# Revit family: PRD_FrankeWS_TltRllHldrs_Heavy-DutyToiletRollHolder_HDTX0001
name_source: partatom
category: Specialty Equipment
revit_build: Autodesk Revit 2018 (Build: 20190510_1515(x64)
units: mm (PartAtom-declared; Revit-internal decimal feet)

## family parameters
Cut with Voids When Loaded = No
Host = Face
OmniClass Number = 23.40.20.21.21
OmniClass Title = Toilet Paper Dispensers
Part Type = Normal
Room Calculation Point = No
Round Connector Dimension = Use Diameter
Shared = No

## types (1)
- HDTX0001
    AssetType = Fixed
    BIMObjectName = PRD_AR_ToiletRollHolders_Heavy-DutyToiletRollHolder_HDTX0001
    Category = Pr_40_20_76_88, Toilet roll holders
    Color = Stainless steel
    Default Elevation = 700 mm  [stored 2.29659 ft]
    Description = Toilet roll holder for wall mounting, stainless steel, surface satin finished, material thickness 14 gauge (2 mm), replaceable spindle secured by heavy-duty lock, for 1 roll with maximum 130 mm width, including stainless steel screws and dowels
    DurationUnit = year
    Features = stainless steel, 2.00 mm, satin finished, wall mounting, 140x110x110 mm (WxHxD)
    FillingQuantity = 1 ROLL
    Finish = Satin finished
    FinishAndColour = Stainless steel, satin finished
    Form = Wall mounted
    GrossWeight = 1.35 kg
    IfcExportAs = IfcFurnitureType
    IfcExportType = NOTDEFINED
    IntegralAccessories = Stainless steel screws and dowels incl.
    MainColor = Stainless steel
    Manufacturer = KWC Group AG
    ManufacturerName = KWC Group AG
    ManufacturerURL = www.kwc.com
    Material = Stainless steel
    Materials = Stainless steel
    MaximumWidthOfConsumable = 130 mm  [stored 0.426509 ft]
    Model = HDTX0001
    ModelNumber = 2030005623
    ModelReference = HDTX0001
    NBSDescription = Toilet roll holders
    NBSReference = 45-35-72/368
    Name = HEAVY-DUTY toilet roll holder HDTX0001
    NetWeight = 1.10 kg
    NominalDepth = 110 mm  [stored 0.360892 ft]
    NominalHeight = 110 mm  [stored 0.360892 ft]
    NominalLength = 140 mm  [stored 0.459318 ft]
    NominalWidth = 140 mm  [stored 0.459318 ft]
    ProductInformation = https://pim.kwc.com
    RollHolderMaterial = PRD_AR_StainlessSteel_SatinFinished
    Size = 140 x 110 x 110 mm
    Style = Toilet roll holder
    ToiletRollMaterial = PRD_AR_ToiletRoll
    URL = www.kwc.com
    Uniclass2015Code = Pr_40_20_76_88
    Uniclass2015Title = Toilet roll holders
    Uniclass2015Version = Products v1.5
    Version = 1
    WarrantyDurationUnit = year

note: [stored X ft] marks values corroborated as IEEE doubles in the binary element streams (Revit-internal decimal feet)

## geometry (parser evidence)
native form markers: Sweep x2
no freeform markers — native parametric forms only
